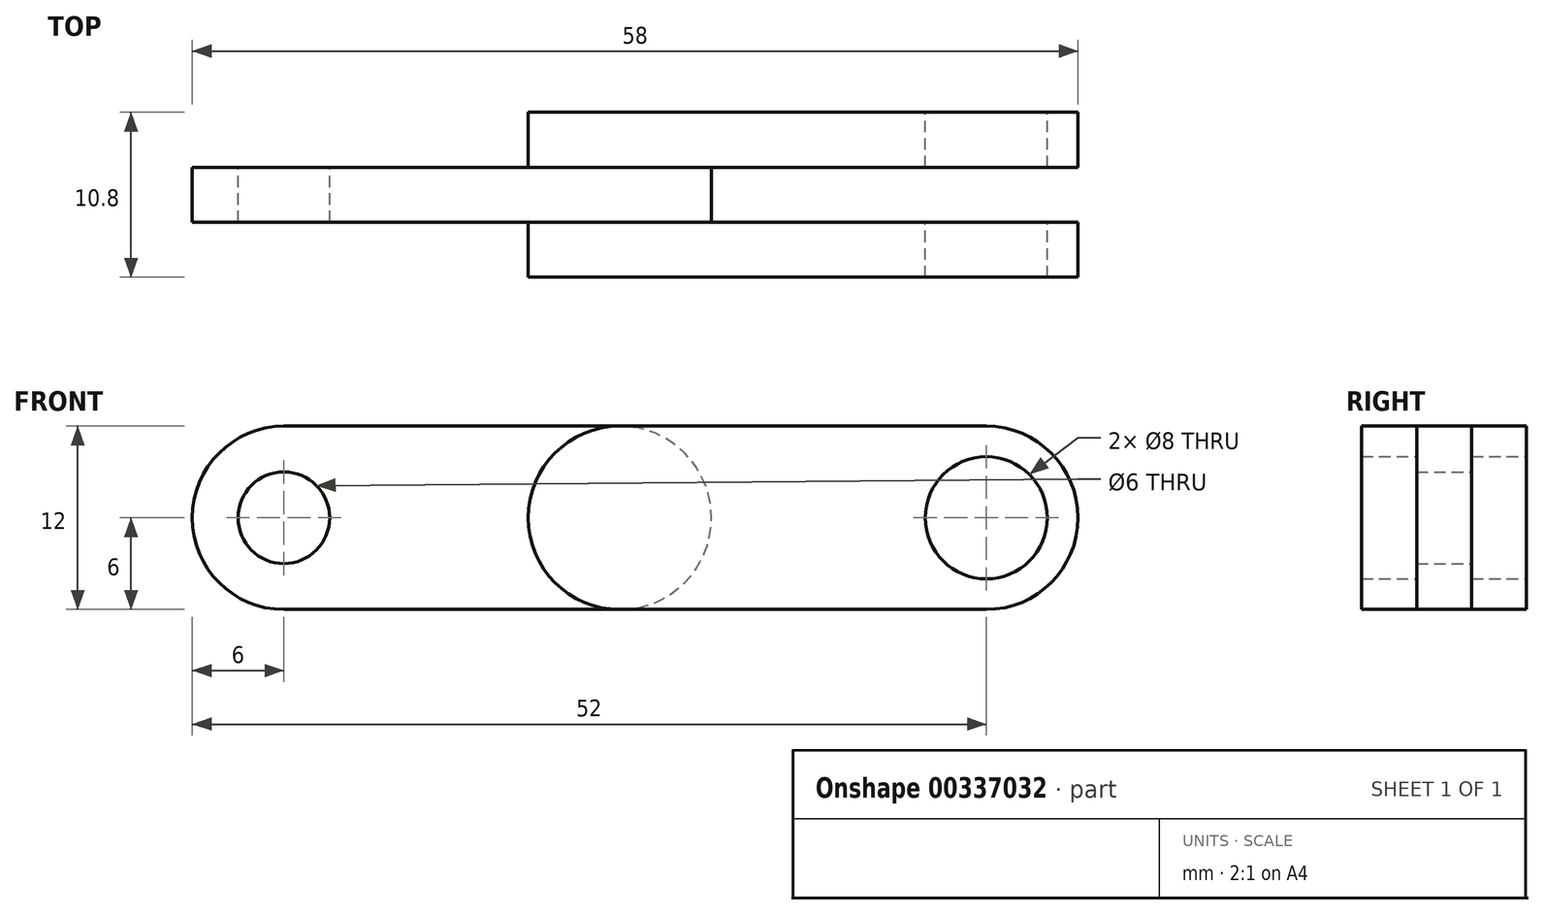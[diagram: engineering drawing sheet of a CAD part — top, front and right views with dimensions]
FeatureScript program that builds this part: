
annotation { "Feature Type Name" : "Feature", "Feature Type Description" : "" }
export const myFeature = defineFeature(function(context is Context, id is Id, definition is map)
    precondition{}
    {
        {
            var Q0;
            Q0=qCreatedBy(makeId("Front.planeOp"),FACE);
            var sketch = newSketch(context, id + "F0", { "sketchPlane" : qUnion([Q0])});
            skLineSegment(sketch, "E0", {"start": v(0, 12) * mm, "end": v(22, 12) * mm});
            skLineSegment(sketch, "E1", {"start": v(0, 0) * mm, "end": v(22, 0) * mm});
            skLineSegment(sketch, "E2", {"start": v(0, 12) * mm, "end": v(0, 0) * mm, "construction": true});
            skLineSegment(sketch, "E3", {"start": v(22, 12) * mm, "end": v(22, 0) * mm, "construction": true});
            skArc(sketch, "E4", {"start": v(0, 12) * mm, "mid": v(-6, 6) * mm, "end": v(0, 0) * mm});
            skArc(sketch, "E5", {"start": v(22, 12) * mm, "mid": v(28, 6) * mm, "end": v(22, 0) * mm});
            skCircle(sketch, "E6", {"center": v(0, 6) * mm, "radius": 3 * mm});
            skSolve(sketch);
        }
        {
            var Q0;
            Q0=makeQuery(id+"F0.imprint","IMPRINT",FACE,{"disambiguationData":[TD([[makeQuery(id+"F0.imprint","IMPRINT",EDGE,{"derivedFrom":sQuery(id+"F0.wireOp",EDGE,"E0")}),-1.0]])]});
            extrude(context, id + "F1", {"entities" : qUnion([Q0]), "depth" : 3.6 * mm});
        }
        {
            var Q0;
            Q0=qCreatedBy(makeId("Front.planeOp"),FACE);
            var sketch = newSketch(context, id + "F2", { "sketchPlane" : qUnion([Q0])});
            skLineSegment(sketch, "E7", {"start": v(22, 12) * mm, "end": v(46, 12) * mm});
            skLineSegment(sketch, "E8", {"start": v(22, 0) * mm, "end": v(46, 0) * mm});
            skLineSegment(sketch, "E9", {"start": v(46, 12) * mm, "end": v(46, 0) * mm, "construction": true});
            skLineSegment(sketch, "E10", {"start": v(22, 12) * mm, "end": v(22, 0) * mm, "construction": true});
            skArc(sketch, "E11", {"start": v(46, 12) * mm, "mid": v(52, 6) * mm, "end": v(46, 0) * mm});
            skArc(sketch, "E12", {"start": v(22, 12) * mm, "mid": v(16, 6) * mm, "end": v(22, 0) * mm});
            skSolve(sketch);
        }
        {
            var Q0;
            Q0 = qSketchRegion(id + "F2", true);
            extrude(context, id + "F3", {"entities" : qUnion([Q0]), "operationType" : NewBodyOperationType.ADD, "oppositeDirection" : true, "depth" : 3.6 * mm});
        }
        {
            var Q0;
            Q0=makeQuery(id+"F1.opExtrude","CAP_FACE",FACE,{"disambiguationData":[OSD([sQuery(id+"F0.wireOp",EDGE,"E0"),sQuery(id+"F0.wireOp",EDGE,"E1"),sQuery(id+"F0.wireOp",EDGE,"E4"),sQuery(id+"F0.wireOp",EDGE,"E5"),sQuery(id+"F0.wireOp",EDGE,"E6")])],"isStart":false});
            var sketch = newSketch(context, id + "F4", { "sketchPlane" : qUnion([Q0])});
            skLineSegment(sketch, "E13", {"start": v(22, 12) * mm, "end": v(46, 12) * mm});
            skLineSegment(sketch, "E14", {"start": v(46, 12) * mm, "end": v(46, 0) * mm, "construction": true});
            skLineSegment(sketch, "E15", {"start": v(46, 0) * mm, "end": v(22, 0) * mm});
            skLineSegment(sketch, "E16", {"start": v(22, 0) * mm, "end": v(22, 12) * mm, "construction": true});
            skArc(sketch, "E17", {"start": v(22, 12) * mm, "mid": v(16, 6) * mm, "end": v(22, 0) * mm});
            skArc(sketch, "E18", {"start": v(46, 12) * mm, "mid": v(52, 6) * mm, "end": v(46, 0) * mm});
            skSolve(sketch);
        }
        {
            var Q0;
            Q0 = qSketchRegion(id + "F4", true);
            extrude(context, id + "F5", {"entities" : qUnion([Q0]), "operationType" : NewBodyOperationType.ADD, "depth" : 3.6 * mm});
        }
        {
            var Q0;
            Q0=makeQuery(id+"F2.imprint","IMPRINT",FACE,{"disambiguationData":[TD([[makeQuery(id+"F2.imprint","IMPRINT",EDGE,{"derivedFrom":sQuery(id+"F2.wireOp",EDGE,"E7")}),-1.0]])]});
            var sketch = newSketch(context, id + "F6", { "sketchPlane" : qUnion([Q0])});
            skCircle(sketch, "E19", {"center": v(46, 6) * mm, "radius": 4 * mm});
            skSolve(sketch);
        }
        {
            var Q0;
            Q0 = qSketchRegion(id + "F6", true);
            extrude(context, id + "F7", {"entities" : qUnion([Q0]), "operationType" : NewBodyOperationType.REMOVE, "endBound" : BoundingType.THROUGH_ALL, "depth" : 25 * mm, "hasSecondDirection" : true, "secondDirectionBound" : SecondDirectionBoundingType.THROUGH_ALL, "secondDirectionOppositeDirection" : true, "secondDirectionDepth" : 25 * mm});
        }
    });
